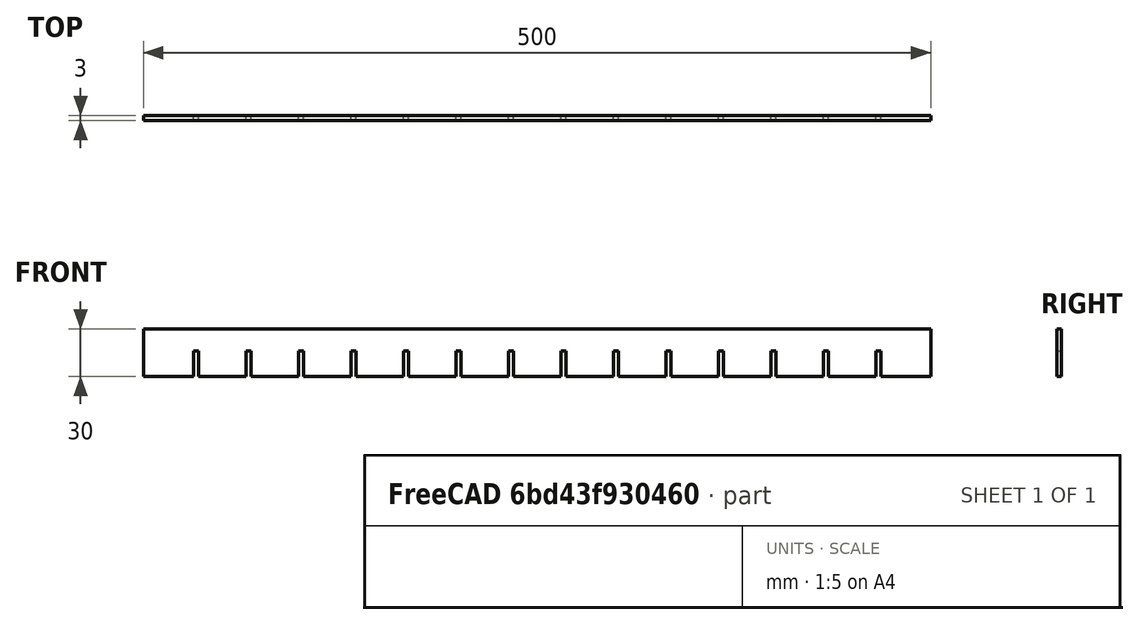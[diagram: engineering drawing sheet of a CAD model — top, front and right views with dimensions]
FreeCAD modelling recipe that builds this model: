
FCSTD DOCUMENT  (FreeCAD 0.16R6686 (Git))
Label: strip_500_extremity
License: CC-BY 3.0
LicenseURL: http://creativecommons.org/licenses/by/3.0/
objects: Part::Box×1, Part::FeaturePython×1, Part::Cut×1
note: 3 computed .brp shape members not serialized (recipe doc carries the construction recipe); baked Part::Feature solids carry a one-line shape summary decoded from their .brp

FEATURE [Part::Box] Box001  label="Hole"
  Height = 16
  Length = 3
  Placement = pos=(31.8333,0,0) rot=(0,0,1;0rad)
  Width = 3
  expr: Placement.Base.x = 100 / 3 - Strip.Width / 2mm
  expr: Height = Strip.Height / 2 + 1mm
  expr: Length = Strip.Width
  expr: Width = Strip.Width
FEATURE [Part::FeaturePython] Array  # Draft array (typed FeaturePython)
  Angle = 360
  ArrayType = 0
  Axis = (1,0,0)
  Base = -> Box001
  Center = (0,0,0)
  IntervalX = (33.3333,0,0)
  IntervalY = (0,1,0)
  IntervalZ = (0,0,1)
  NumberPolar = 1
  NumberX = 14
  NumberY = 0
  NumberZ = 0
  expr: IntervalX.x = 100 / 3
FEATURE [Part::Cut] Cut
  Tool = -> Array
